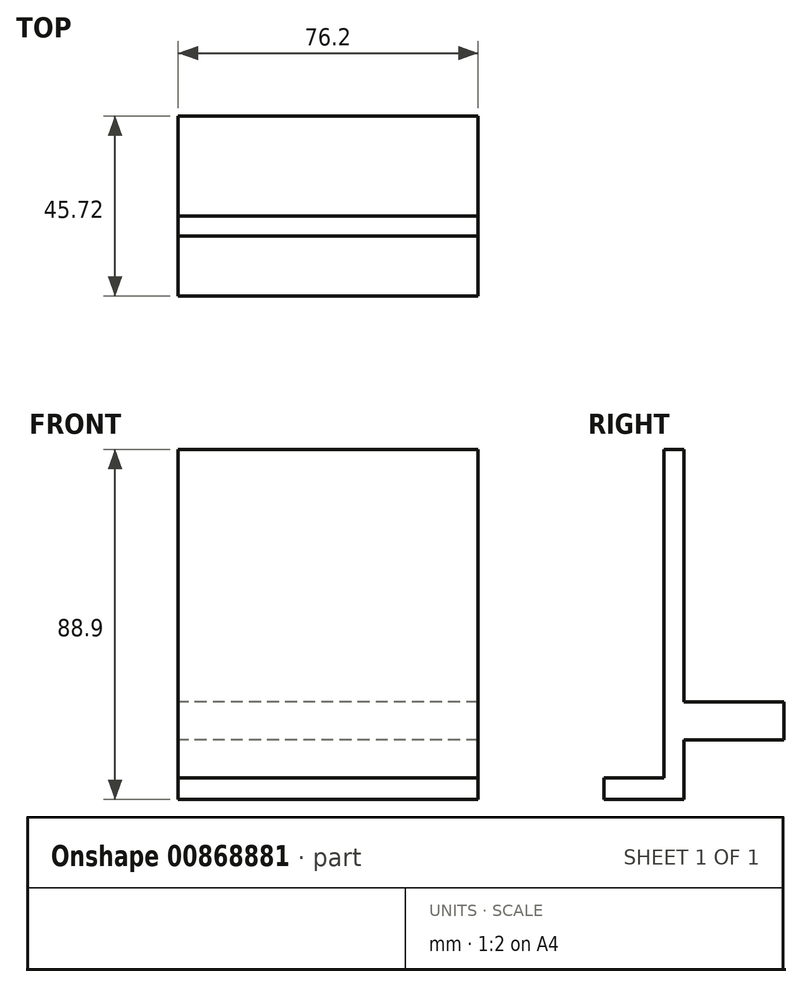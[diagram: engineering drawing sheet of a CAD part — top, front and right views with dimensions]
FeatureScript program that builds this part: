
annotation { "Feature Type Name" : "Feature", "Feature Type Description" : "" }
export const myFeature = defineFeature(function(context is Context, id is Id, definition is map)
    precondition{}
    {
        {
            var Q0;
            Q0=qCreatedBy(makeId("Front.planeOp"),FACE);
            var sketch = newSketch(context, id + "F0", { "sketchPlane" : qUnion([Q0])});
            skLineSegment(sketch, "E0.bottom", {"start": v(-38.1, 44.45) * mm, "end": v(38.1, 44.45) * mm});
            skLineSegment(sketch, "E0.top", {"start": v(-38.1, -44.45) * mm, "end": v(38.1, -44.45) * mm});
            skLineSegment(sketch, "E0.left", {"start": v(-38.1, 44.45) * mm, "end": v(-38.1, -44.45) * mm});
            skLineSegment(sketch, "E0.right", {"start": v(38.1, 44.45) * mm, "end": v(38.1, -44.45) * mm});
            skLineSegment(sketch, "E1", {"start": v(-38.1, 0) * mm, "end": v(38.1, 0) * mm, "construction": true});
            skLineSegment(sketch, "E2", {"start": v(0, 44.45) * mm, "end": v(0, -44.45) * mm, "construction": true});
            skSolve(sketch);
        }
        {
            var Q0;
            Q0 = qSketchRegion(id + "F0", true);
            extrude(context, id + "F1", {"entities" : qUnion([Q0]), "depth" : 5.08 * mm, "offsetDistance" : 25.4 * mm});
        }
        {
            var Q0;
            Q0=makeQuery(id+"F1.opExtrude","CAP_FACE",FACE,{"disambiguationData":[OSD([sQuery(id+"F0.wireOp",EDGE,"E0.bottom"),sQuery(id+"F0.wireOp",EDGE,"E0.top"),sQuery(id+"F0.wireOp",EDGE,"E0.left"),sQuery(id+"F0.wireOp",EDGE,"E0.right")])],"isStart":false});
            var sketch = newSketch(context, id + "F2", { "sketchPlane" : qUnion([Q0])});
            skLineSegment(sketch, "E3.bottom", {"start": v(-38.1, -38.93) * mm, "end": v(38.1, -38.93) * mm});
            skLineSegment(sketch, "E3.top", {"start": v(-38.1, -44.45) * mm, "end": v(38.1, -44.45) * mm});
            skLineSegment(sketch, "E3.left", {"start": v(-38.1, -38.93) * mm, "end": v(-38.1, -44.45) * mm});
            skLineSegment(sketch, "E3.right", {"start": v(38.1, -38.93) * mm, "end": v(38.1, -44.45) * mm});
            skSolve(sketch);
        }
        {
            var Q0;
            Q0 = qSketchRegion(id + "F2", true);
            extrude(context, id + "F3", {"entities" : qUnion([Q0]), "operationType" : NewBodyOperationType.ADD, "depth" : 15.24 * mm, "offsetDistance" : 25.4 * mm});
        }
        {
            var Q0;
            Q0=makeQuery(id+"F1.opExtrude","CAP_FACE",FACE,{"disambiguationData":[OSD([sQuery(id+"F0.wireOp",EDGE,"E0.bottom"),sQuery(id+"F0.wireOp",EDGE,"E0.top"),sQuery(id+"F0.wireOp",EDGE,"E0.left"),sQuery(id+"F0.wireOp",EDGE,"E0.right")])],"isStart":true});
            var sketch = newSketch(context, id + "F4", { "sketchPlane" : qUnion([Q0])});
            skLineSegment(sketch, "E4.bottom", {"start": v(-38.1, -19.7) * mm, "end": v(38.1, -19.7) * mm});
            skLineSegment(sketch, "E4.top", {"start": v(-38.1, -29.3) * mm, "end": v(38.1, -29.3) * mm});
            skLineSegment(sketch, "E4.left", {"start": v(-38.1, -19.7) * mm, "end": v(-38.1, -29.3) * mm});
            skLineSegment(sketch, "E4.right", {"start": v(38.1, -19.7) * mm, "end": v(38.1, -29.3) * mm});
            skSolve(sketch);
        }
        {
            var Q0;
            Q0 = qSketchRegion(id + "F4", true);
            extrude(context, id + "F5", {"entities" : qUnion([Q0]), "operationType" : NewBodyOperationType.ADD, "depth" : 25.4 * mm, "offsetDistance" : 25.4 * mm});
        }
    });
